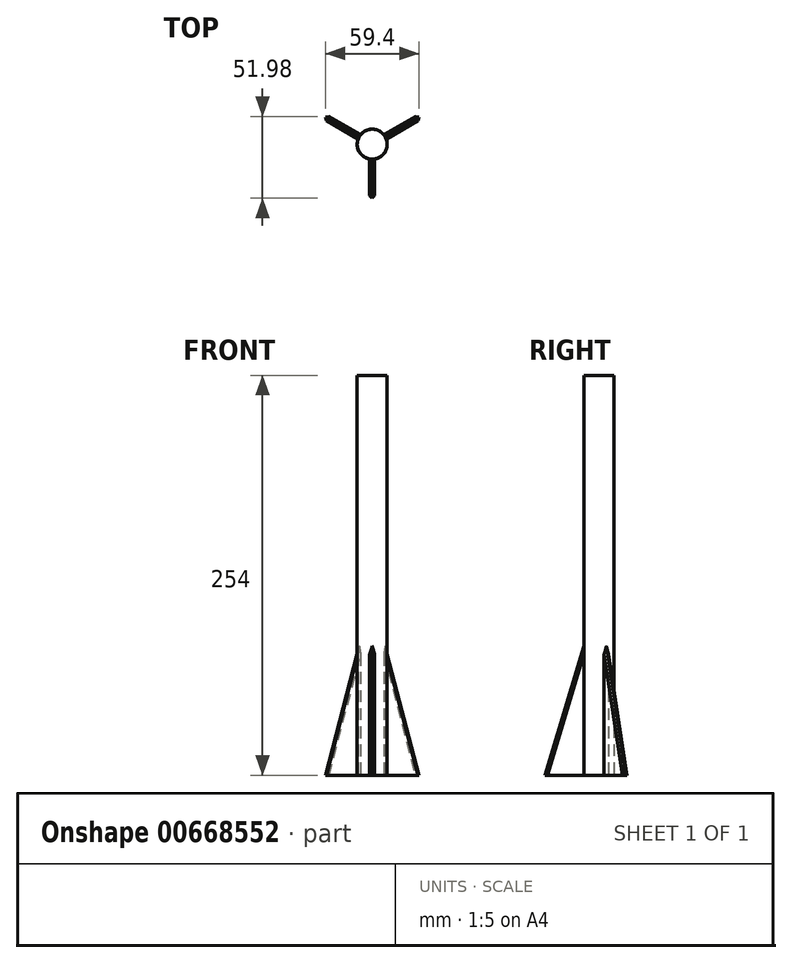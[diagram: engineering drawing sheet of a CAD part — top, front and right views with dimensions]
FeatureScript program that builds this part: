
annotation { "Feature Type Name" : "Feature", "Feature Type Description" : "" }
export const myFeature = defineFeature(function(context is Context, id is Id, definition is map)
    precondition{}
    {
        {
            var Q0;
            Q0=qCreatedBy(makeId("Top.planeOp"),FACE);
            var sketch = newSketch(context, id + "F0", { "sketchPlane" : qUnion([Q0])});
            skCircle(sketch, "E0", {"center": v(0, 0) * mm, "radius": 9.53 * mm});
            skSolve(sketch);
        }
        {
            var Q0;
            Q0=qSketchRegion(id+"F0",true);
            extrude(context, id + "F1", {"entities" : qUnion([Q0]), "depth" : 254 * mm, "offsetDistance" : 25.4 * mm});
        }
        {
            var Q0;
            Q0=qCreatedBy(makeId("Right.planeOp"),FACE);
            var sketch = newSketch(context, id + "F2", { "sketchPlane" : qUnion([Q0])});
            skLineSegment(sketch, "E1", {"start": v(-9.53, 0) * mm, "end": v(-9.53, 254) * mm});
            skLineSegment(sketch, "E2", {"start": v(9.53, 254) * mm, "end": v(9.53, 0) * mm});
            skLineSegment(sketch, "E3", {"start": v(-9.53, 83.56) * mm, "end": v(-34.76, 0) * mm});
            skLineSegment(sketch, "E4", {"start": v(-34.76, 0) * mm, "end": v(-9.53, 0) * mm});
            skLineSegment(sketch, "E5", {"start": v(-9.52, 83.56) * mm, "end": v(-6.31, 83.56) * mm});
            skLineSegment(sketch, "E6", {"start": v(-6.31, 83.56) * mm, "end": v(-6.31, 0) * mm});
            skLineSegment(sketch, "E7", {"start": v(-6.31, 0) * mm, "end": v(-9.53, 0) * mm});
            skSolve(sketch);
        }
        {
            var Q0;
            Q0=qSketchRegion(id+"F2",true);
            extrude(context, id + "F3", {"entities" : qUnion([Q0]), "operationType" : NewBodyOperationType.ADD, "endBound" : BoundingType.SYMMETRIC, "depth" : 3.17 * mm, "offsetDistance" : 25.4 * mm});
        }
        {
            var Q0;
            Q0=makeQuery(id+"F3.opExtrude","CAP_EDGE",EDGE,{"disambiguationData":[OSD([sQuery(id+"F2.wireOp",EDGE,"E3")])],"isStart":false});
            var Q1;
            Q1=makeQuery(id+"F3.opExtrude","CAP_EDGE",EDGE,{"disambiguationData":[OSD([sQuery(id+"F2.wireOp",EDGE,"E3")])],"isStart":true});
            chamfer(context, id + "F4", {"entities" : qUnion([Q0, Q1]), "width" : 2.03 * mm, "tangentPropagation" : true});
        }
        {
            var Q0;
            Q0=makeQuery(id+"F1.opExtrude","SWEPT_BODY",BODY,{"disambiguationData":[OSD([sQuery(id+"F0.wireOp",EDGE,"E0")])]});
            var Q1;
            Q1=makeQuery(id+"F1.opExtrude","SWEPT_FACE",FACE,{"disambiguationData":[OSD([sQuery(id+"F0.wireOp",EDGE,"E0")])]});
            circularPattern(context, id + "F5", {"entities" : qUnion([Q0]), "axis" : qUnion([Q1]), "angle" : 360 * degree, "instanceCount" : 3, "equalSpace" : true});
        }
    });
